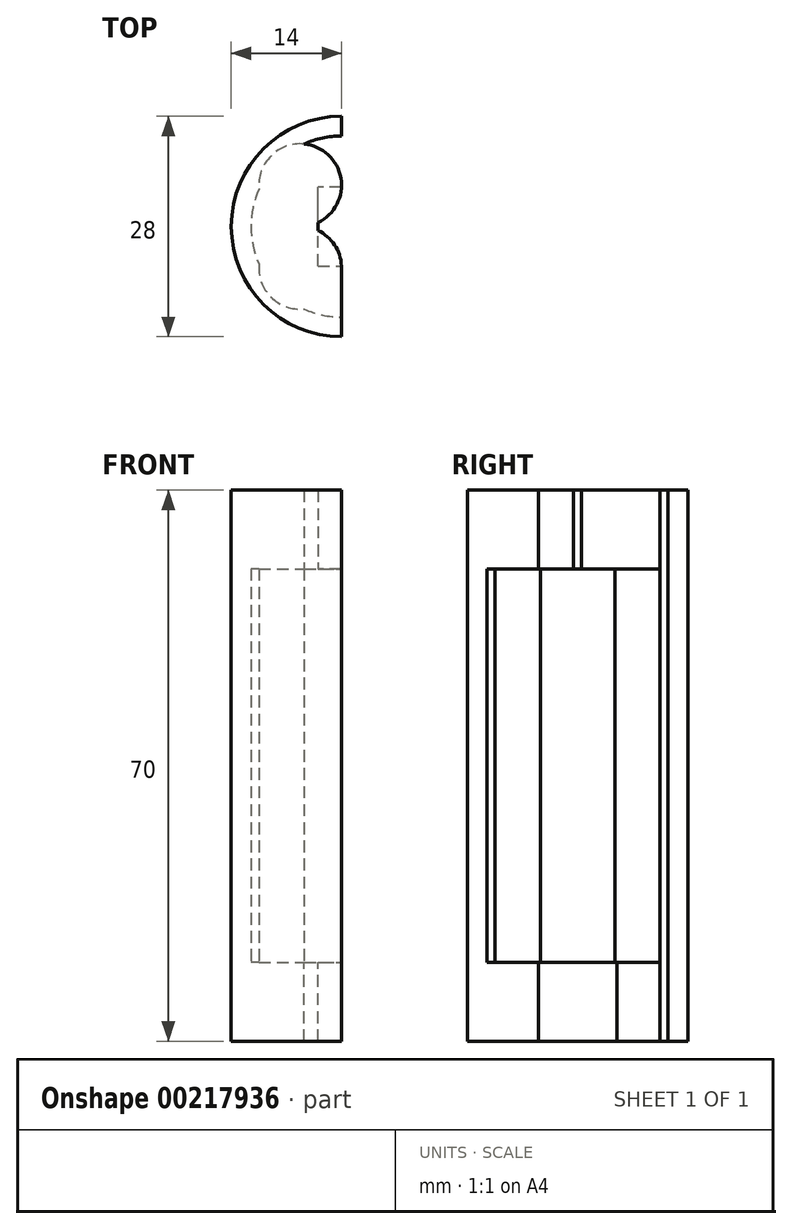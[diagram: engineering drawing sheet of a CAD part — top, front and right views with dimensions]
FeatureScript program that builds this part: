
annotation { "Feature Type Name" : "Feature", "Feature Type Description" : "" }
export const myFeature = defineFeature(function(context is Context, id is Id, definition is map)
    precondition{}
    {
        {
            var Q0;
            Q0=qCreatedBy(makeId("Top.planeOp"),FACE);
            var sketch = newSketch(context, id + "F0", { "sketchPlane" : qUnion([Q0])});
            skCircle(sketch, "E0", {"center": v(0, 0) * mm, "radius": 14 * mm});
            skLineSegment(sketch, "E1", {"start": v(0, 0) * mm, "end": v(0, -9) * mm});
            skLineSegment(sketch, "E2", {"start": v(0, -9) * mm, "end": v(0, -14) * mm});
            skLineSegment(sketch, "E3", {"start": v(0, 9) * mm, "end": v(0, 14) * mm});
            skLineSegment(sketch, "E4", {"start": v(0, 0) * mm, "end": v(0, 9) * mm});
            skLineSegment(sketch, "E5.left", {"start": v(0, 9) * mm, "end": v(0, 6) * mm});
            skLineSegment(sketch, "E6.top", {"start": v(0, 5) * mm, "end": v(-3, 5) * mm});
            skLineSegment(sketch, "E6.left", {"start": v(0, -5) * mm, "end": v(0, 5) * mm});
            skLineSegment(sketch, "E6.right", {"start": v(-3, -5) * mm, "end": v(-3, 5) * mm});
            skPoint(sketch, "E7.0.midPoint", {"position": v(-3.18, 0) * mm});
            skCircle(sketch, "E8", {"center": v(0, 0) * mm, "radius": 11.5 * mm});
            skPoint(sketch, "E9.0.midPoint", {"position": v(-5, 0) * mm});
            skLineSegment(sketch, "E10", {"start": v(-3, -5) * mm, "end": v(0, -5) * mm});
            skCircle(sketch, "E11.cCircle", {"center": v(0, 0) * mm, "radius": 5.25 * mm, "construction": true});
            skLineSegment(sketch, "E11.0", {"start": v(-5.25, -5.25) * mm, "end": v(-5.25, 5.25) * mm});
            skLineSegment(sketch, "E11.1", {"start": v(-5.25, 5.25) * mm, "end": v(5.25, 5.25) * mm});
            skLineSegment(sketch, "E11.2", {"start": v(5.25, 5.25) * mm, "end": v(5.25, -5.25) * mm});
            skLineSegment(sketch, "E11.3", {"start": v(5.25, -5.25) * mm, "end": v(-5.25, -5.25) * mm});
            skPoint(sketch, "E11.0.midPoint", {"position": v(-5.25, 0) * mm});
            skCircle(sketch, "E12", {"center": v(-5.25, -5.25) * mm, "radius": 5.25 * mm});
            skCircle(sketch, "E13", {"center": v(-5.25, 5.25) * mm, "radius": 5.25 * mm});
            skSolve(sketch);
        }
        {
            var Q0;
            {var subQ0=sQuery(id+"F0.wireOp",EDGE,"E2");var subQ1=sQuery(id+"F0.wireOp",EDGE,"E0");var subQ2=makeQuery(id+"F0.imprint","INTERSECT",VERTEX,{"derivedFrom":[subQ1,subQ0]});Q0=makeQuery(id+"F0.imprint","IMPRINT",FACE,{"disambiguationData":[TD([[makeQuery(id+"F0.imprint","IMPRINT",EDGE,{"disambiguationData":[TD([[subQ2,1.0]])],"derivedFrom":subQ1}),1.0]])]});}
            var Q1;
            {var subQ1=sQuery(id+"F0.wireOp",EDGE,"E2");var subQ5=sQuery(id+"F0.wireOp",EDGE,"E1");var subQ6=makeQuery(id+"F0.imprint","INTERSECT",VERTEX,{"derivedFrom":[subQ5,subQ1]});Q1=makeQuery(id+"F0.imprint","IMPRINT",FACE,{"disambiguationData":[TD([[makeQuery(id+"F0.imprint","IMPRINT",EDGE,{"disambiguationData":[TD([[subQ6,1.0]])],"derivedFrom":subQ5}),-1.0]])]});}
            var Q2;
            {var subQ6=sQuery(id+"F0.wireOp",EDGE,"E10");var subQ7=sQuery(id+"F0.wireOp",EDGE,"E6.right");var subQ8=makeQuery(id+"F0.imprint","INTERSECT",VERTEX,{"derivedFrom":[subQ7,subQ6]});Q2=makeQuery(id+"F0.imprint","IMPRINT",FACE,{"disambiguationData":[TD([[makeQuery(id+"F0.imprint","IMPRINT",EDGE,{"disambiguationData":[TD([[subQ8,-1.0]])],"derivedFrom":subQ7}),1.0]])]});}
            var Q3;
            {var subQ0=sQuery(id+"F0.wireOp",EDGE,"E12");var subQ1=sQuery(id+"F0.wireOp",EDGE,"E8");var subQ2=makeQuery(id+"F0.imprint","INTERSECT",VERTEX,{"disambiguationData":[OD(0.0)],"derivedFrom":[subQ1,subQ0]});Q3=makeQuery(id+"F0.imprint","IMPRINT",FACE,{"disambiguationData":[TD([[makeQuery(id+"F0.imprint","IMPRINT",EDGE,{"disambiguationData":[TD([[subQ2,-1.0]])],"derivedFrom":subQ1}),1.0]])]});}
            var Q4;
            {var subQ0=sQuery(id+"F0.wireOp",EDGE,"E13");var subQ1=sQuery(id+"F0.wireOp",EDGE,"E8");var subQ2=makeQuery(id+"F0.imprint","INTERSECT",VERTEX,{"disambiguationData":[OD(1.0)],"derivedFrom":[subQ1,subQ0]});Q4=makeQuery(id+"F0.imprint","IMPRINT",FACE,{"disambiguationData":[TD([[makeQuery(id+"F0.imprint","IMPRINT",EDGE,{"disambiguationData":[TD([[subQ2,-1.0]])],"derivedFrom":subQ1}),1.0]])]});}
            var Q5;
            {var subQ0=sQuery(id+"F0.wireOp",EDGE,"E12");var subQ1=sQuery(id+"F0.wireOp",EDGE,"E6.right");var subQ2=makeQuery(id+"F0.imprint","INTERSECT",VERTEX,{"derivedFrom":[subQ1,subQ0]});Q5=makeQuery(id+"F0.imprint","IMPRINT",FACE,{"disambiguationData":[TD([[makeQuery(id+"F0.imprint","IMPRINT",EDGE,{"disambiguationData":[TD([[subQ2,-1.0]])],"derivedFrom":subQ1}),1.0]])]});}
            var Q6;
            {var subQ0=sQuery(id+"F0.wireOp",EDGE,"E13");var subQ1=sQuery(id+"F0.wireOp",EDGE,"E8");var subQ2=makeQuery(id+"F0.imprint","INTERSECT",VERTEX,{"disambiguationData":[OD(0.0)],"derivedFrom":[subQ1,subQ0]});Q6=makeQuery(id+"F0.imprint","IMPRINT",FACE,{"disambiguationData":[TD([[makeQuery(id+"F0.imprint","IMPRINT",EDGE,{"disambiguationData":[TD([[subQ2,-1.0]])],"derivedFrom":subQ1}),1.0]])]});}
            var Q7;
            {var subQ5=sQuery(id+"F0.wireOp",EDGE,"E5.left");Q7=makeQuery(id+"F0.imprint","IMPRINT",FACE,{"disambiguationData":[TD([[makeQuery(id+"F0.imprint","IMPRINT",EDGE,{"derivedFrom":subQ5}),-1.0]])]});}
            var Q8;
            {var subQ0=sQuery(id+"F0.wireOp",EDGE,"E13");var subQ1=sQuery(id+"F0.wireOp",EDGE,"E8");var subQ2=makeQuery(id+"F0.imprint","INTERSECT",VERTEX,{"disambiguationData":[OD(0.0)],"derivedFrom":[subQ1,subQ0]});Q8=makeQuery(id+"F0.imprint","IMPRINT",FACE,{"disambiguationData":[TD([[makeQuery(id+"F0.imprint","IMPRINT",EDGE,{"disambiguationData":[TD([[subQ2,-1.0]])],"derivedFrom":subQ1}),-1.0]])]});}
            var Q9;
            {var subQ0=sQuery(id+"F0.wireOp",EDGE,"E12");var subQ1=sQuery(id+"F0.wireOp",EDGE,"E8");var subQ2=makeQuery(id+"F0.imprint","INTERSECT",VERTEX,{"disambiguationData":[OD(0.0)],"derivedFrom":[subQ1,subQ0]});Q9=makeQuery(id+"F0.imprint","IMPRINT",FACE,{"disambiguationData":[TD([[makeQuery(id+"F0.imprint","IMPRINT",EDGE,{"disambiguationData":[TD([[subQ2,-1.0]])],"derivedFrom":subQ1}),-1.0]])]});}
            var Q10;
            {var subQ0=sQuery(id+"F0.wireOp",EDGE,"E6.right");var subQ1=sQuery(id+"F0.wireOp",EDGE,"E6.top");var subQ2=makeQuery(id+"F0.imprint","INTERSECT",VERTEX,{"derivedFrom":[subQ1,subQ0]});Q10=makeQuery(id+"F0.imprint","IMPRINT",FACE,{"disambiguationData":[TD([[makeQuery(id+"F0.imprint","IMPRINT",EDGE,{"disambiguationData":[TD([[subQ2,1.0]])],"derivedFrom":subQ1}),-1.0]])]});}
            var Q11;
            {var subQ1=sQuery(id+"F0.wireOp",EDGE,"E4");var subQ3=sQuery(id+"F0.wireOp",EDGE,"E11.1");var subQ4=makeQuery(id+"F0.imprint","INTERSECT",VERTEX,{"derivedFrom":[subQ1,subQ3]});Q11=makeQuery(id+"F0.imprint","IMPRINT",FACE,{"disambiguationData":[TD([[makeQuery(id+"F0.imprint","IMPRINT",EDGE,{"disambiguationData":[TD([[subQ4,1.0]])],"derivedFrom":subQ3}),-1.0]])]});}
            var Q12;
            {var subQ1=sQuery(id+"F0.wireOp",EDGE,"E1");var subQ3=sQuery(id+"F0.wireOp",EDGE,"E11.3");var subQ4=makeQuery(id+"F0.imprint","INTERSECT",VERTEX,{"derivedFrom":[subQ1,subQ3]});Q12=makeQuery(id+"F0.imprint","IMPRINT",FACE,{"disambiguationData":[TD([[makeQuery(id+"F0.imprint","IMPRINT",EDGE,{"disambiguationData":[TD([[subQ4,-1.0]])],"derivedFrom":subQ3}),-1.0]])]});}
            extrude(context, id + "F1", {"entities" : qUnion([Q0, Q1, Q2, Q3, Q4, Q5, Q6, Q7, Q8, Q9, Q10, Q11, Q12]), "oppositeDirection" : true, "depth" : 10 * mm});
        }
        {
            var Q0;
            {var subQ0=sQuery(id+"F0.wireOp",EDGE,"E2");var subQ1=sQuery(id+"F0.wireOp",EDGE,"E0");var subQ2=makeQuery(id+"F0.imprint","INTERSECT",VERTEX,{"derivedFrom":[subQ1,subQ0]});Q0=makeQuery(id+"F0.imprint","IMPRINT",FACE,{"disambiguationData":[TD([[makeQuery(id+"F0.imprint","IMPRINT",EDGE,{"disambiguationData":[TD([[subQ2,1.0]])],"derivedFrom":subQ1}),1.0]])]});}
            extrude(context, id + "F2", {"entities" : qUnion([Q0]), "operationType" : NewBodyOperationType.ADD, "depth" : 50 * mm});
        }
        {
            var Q0;
            Q0=makeQuery(id+"F2.opExtrude","CAP_FACE",FACE,{"disambiguationData":[OSD([sQuery(id+"F0.wireOp",EDGE,"E0"),sQuery(id+"F0.wireOp",EDGE,"oU96YchA-BZAO-iMHW-yuLs-znTI9j7FRH7l.top"),sQuery(id+"F0.wireOp",EDGE,"6tNbldtE-jyNb-ox46-p6dI-xDiLGx6BKobI"),sQuery(id+"F0.wireOp",EDGE,"gYREm4CE-hqkD-VulL-Gk3Q-KIUnsvQmfiCx"),sQuery(id+"F0.wireOp",EDGE,"E2"),sQuery(id+"F0.wireOp",EDGE,"E3"),sQuery(id+"F0.wireOp",EDGE,"hiq0YSxW-zsfy-ITCv-7inL-48aoCokMUDRA")])],"isStart":false});
            extrude(context, id + "F3", {"entities" : qUnion([Q0]), "operationType" : NewBodyOperationType.ADD, "depth" : 10 * mm});
        }
        {
            var Q0;
            Q0=makeQuery(id+"F0.imprint","IMPRINT",FACE,{"disambiguationData":[TD([[makeQuery(id+"F0.imprint","IMPRINT",EDGE,{"derivedFrom":sQuery(id+"F0.wireOp",EDGE,"oU96YchA-BZAO-iMHW-yuLs-znTI9j7FRH7l.top")}),1.0]])]});
            var Q1;
            Q1=makeQuery(id+"F0.imprint","IMPRINT",FACE,{"disambiguationData":[TD([[makeQuery(id+"F0.imprint","IMPRINT",EDGE,{"derivedFrom":sQuery(id+"F0.wireOp",EDGE,"E5.bottom")}),1.0]])]});
            var Q2;
            Q2=makeQuery(id+"F0.imprint","IMPRINT",FACE,{"disambiguationData":[TD([[makeQuery(id+"F0.imprint","IMPRINT",EDGE,{"derivedFrom":sQuery(id+"F0.wireOp",EDGE,"E6.bottom")}),-1.0]])]});
            var Q3;
            {var subQ5=sQuery(id+"F0.wireOp",EDGE,"E1");Q3=makeQuery(id+"F0.imprint","IMPRINT",FACE,{"disambiguationData":[TD([[makeQuery(id+"F0.imprint","IMPRINT",EDGE,{"derivedFrom":subQ5}),-1.0]])]});}
            var Q4;
            Q4=makeQuery(id+"F0.imprint","IMPRINT",FACE,{"disambiguationData":[TD([[makeQuery(id+"F0.imprint","IMPRINT",EDGE,{"derivedFrom":sQuery(id+"F0.wireOp",EDGE,"E6.top")}),1.0]])]});
            var Q5;
            {var subQ0=sQuery(id+"F0.wireOp",EDGE,"E12");var subQ1=sQuery(id+"F0.wireOp",EDGE,"E8");var subQ2=makeQuery(id+"F0.imprint","INTERSECT",VERTEX,{"disambiguationData":[OD(0.0)],"derivedFrom":[subQ1,subQ0]});Q5=makeQuery(id+"F0.imprint","IMPRINT",FACE,{"disambiguationData":[TD([[makeQuery(id+"F0.imprint","IMPRINT",EDGE,{"disambiguationData":[TD([[subQ2,-1.0]])],"derivedFrom":subQ1}),-1.0]])]});}
            var Q6;
            {var subQ0=sQuery(id+"F0.wireOp",EDGE,"E13");var subQ1=sQuery(id+"F0.wireOp",EDGE,"E8");var subQ2=makeQuery(id+"F0.imprint","INTERSECT",VERTEX,{"disambiguationData":[OD(0.0)],"derivedFrom":[subQ1,subQ0]});Q6=makeQuery(id+"F0.imprint","IMPRINT",FACE,{"disambiguationData":[TD([[makeQuery(id+"F0.imprint","IMPRINT",EDGE,{"disambiguationData":[TD([[subQ2,-1.0]])],"derivedFrom":subQ1}),-1.0]])]});}
            var Q7;
            {var subQ5=sQuery(id+"F0.wireOp",EDGE,"E5.left");Q7=makeQuery(id+"F0.imprint","IMPRINT",FACE,{"disambiguationData":[TD([[makeQuery(id+"F0.imprint","IMPRINT",EDGE,{"derivedFrom":subQ5}),-1.0]])]});}
            var Q8;
            {var subQ0=sQuery(id+"F0.wireOp",EDGE,"E13");var subQ1=sQuery(id+"F0.wireOp",EDGE,"E8");var subQ2=makeQuery(id+"F0.imprint","INTERSECT",VERTEX,{"disambiguationData":[OD(0.0)],"derivedFrom":[subQ1,subQ0]});Q8=makeQuery(id+"F0.imprint","IMPRINT",FACE,{"disambiguationData":[TD([[makeQuery(id+"F0.imprint","IMPRINT",EDGE,{"disambiguationData":[TD([[subQ2,-1.0]])],"derivedFrom":subQ1}),1.0]])]});}
            var Q9;
            {var subQ0=sQuery(id+"F0.wireOp",EDGE,"E13");var subQ1=sQuery(id+"F0.wireOp",EDGE,"E8");var subQ2=makeQuery(id+"F0.imprint","INTERSECT",VERTEX,{"disambiguationData":[OD(1.0)],"derivedFrom":[subQ1,subQ0]});Q9=makeQuery(id+"F0.imprint","IMPRINT",FACE,{"disambiguationData":[TD([[makeQuery(id+"F0.imprint","IMPRINT",EDGE,{"disambiguationData":[TD([[subQ2,-1.0]])],"derivedFrom":subQ1}),1.0]])]});}
            var Q10;
            {var subQ0=sQuery(id+"F0.wireOp",EDGE,"E12");var subQ1=sQuery(id+"F0.wireOp",EDGE,"E8");var subQ2=makeQuery(id+"F0.imprint","INTERSECT",VERTEX,{"disambiguationData":[OD(0.0)],"derivedFrom":[subQ1,subQ0]});Q10=makeQuery(id+"F0.imprint","IMPRINT",FACE,{"disambiguationData":[TD([[makeQuery(id+"F0.imprint","IMPRINT",EDGE,{"disambiguationData":[TD([[subQ2,-1.0]])],"derivedFrom":subQ1}),1.0]])]});}
            var Q11;
            {var subQ0=sQuery(id+"F0.wireOp",EDGE,"E12");var subQ1=sQuery(id+"F0.wireOp",EDGE,"E6.right");var subQ2=makeQuery(id+"F0.imprint","INTERSECT",VERTEX,{"derivedFrom":[subQ1,subQ0]});Q11=makeQuery(id+"F0.imprint","IMPRINT",FACE,{"disambiguationData":[TD([[makeQuery(id+"F0.imprint","IMPRINT",EDGE,{"disambiguationData":[TD([[subQ2,-1.0]])],"derivedFrom":subQ1}),1.0]])]});}
            var Q12;
            {var subQ0=sQuery(id+"F0.wireOp",EDGE,"E6.right");var subQ1=sQuery(id+"F0.wireOp",EDGE,"E6.top");var subQ2=makeQuery(id+"F0.imprint","INTERSECT",VERTEX,{"derivedFrom":[subQ1,subQ0]});Q12=makeQuery(id+"F0.imprint","IMPRINT",FACE,{"disambiguationData":[TD([[makeQuery(id+"F0.imprint","IMPRINT",EDGE,{"disambiguationData":[TD([[subQ2,1.0]])],"derivedFrom":subQ1}),-1.0]])]});}
            var Q13;
            {var subQ6=sQuery(id+"F0.wireOp",EDGE,"E10");var subQ7=sQuery(id+"F0.wireOp",EDGE,"E6.right");var subQ8=makeQuery(id+"F0.imprint","INTERSECT",VERTEX,{"derivedFrom":[subQ7,subQ6]});Q13=makeQuery(id+"F0.imprint","IMPRINT",FACE,{"disambiguationData":[TD([[makeQuery(id+"F0.imprint","IMPRINT",EDGE,{"disambiguationData":[TD([[subQ8,-1.0]])],"derivedFrom":subQ7}),1.0]])]});}
            var Q14;
            {var subQ0=sQuery(id+"F0.wireOp",EDGE,"E10");var subQ1=sQuery(id+"F0.wireOp",EDGE,"E6.right");var subQ2=makeQuery(id+"F0.imprint","INTERSECT",VERTEX,{"derivedFrom":[subQ1,subQ0]});Q14=makeQuery(id+"F0.imprint","IMPRINT",FACE,{"disambiguationData":[TD([[makeQuery(id+"F0.imprint","IMPRINT",EDGE,{"disambiguationData":[TD([[subQ2,-1.0]])],"derivedFrom":subQ1}),-1.0]])]});}
            var Q15;
            {var subQ5=sQuery(id+"F0.wireOp",EDGE,"E6.left");Q15=makeQuery(id+"F0.imprint","IMPRINT",FACE,{"disambiguationData":[TD([[makeQuery(id+"F0.imprint","IMPRINT",EDGE,{"derivedFrom":subQ5}),1.0]])]});}
            var Q16;
            {var subQ1=sQuery(id+"F0.wireOp",EDGE,"E2");var subQ5=sQuery(id+"F0.wireOp",EDGE,"E1");var subQ6=makeQuery(id+"F0.imprint","INTERSECT",VERTEX,{"derivedFrom":[subQ5,subQ1]});Q16=makeQuery(id+"F0.imprint","IMPRINT",FACE,{"disambiguationData":[TD([[makeQuery(id+"F0.imprint","IMPRINT",EDGE,{"disambiguationData":[TD([[subQ6,1.0]])],"derivedFrom":subQ5}),-1.0]])]});}
            var Q17;
            {var subQ1=sQuery(id+"F0.wireOp",EDGE,"E4");var subQ3=sQuery(id+"F0.wireOp",EDGE,"E11.1");var subQ4=makeQuery(id+"F0.imprint","INTERSECT",VERTEX,{"derivedFrom":[subQ1,subQ3]});Q17=makeQuery(id+"F0.imprint","IMPRINT",FACE,{"disambiguationData":[TD([[makeQuery(id+"F0.imprint","IMPRINT",EDGE,{"disambiguationData":[TD([[subQ4,1.0]])],"derivedFrom":subQ3}),-1.0]])]});}
            extrude(context, id + "F4", {"entities" : qUnion([Q0, Q1, Q2, Q3, Q4, Q5, Q6, Q7, Q8, Q9, Q10, Q11, Q12, Q13, Q14, Q15, Q16, Q17]), "operationType" : NewBodyOperationType.ADD, "depth" : 60 * mm, "hasSecondDirection" : true, "secondDirectionOppositeDirection" : false, "secondDirectionDepth" : 50 * mm});
        }
    });
